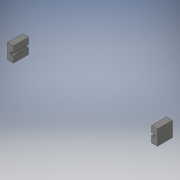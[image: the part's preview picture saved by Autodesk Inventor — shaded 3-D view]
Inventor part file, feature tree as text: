
AUTODESK INVENTOR PART (.ipt)
format: ipt  version: 2018 (Build 220112000, 112)  size: 122,368 bytes
history: native  units: in
note: dims shown in document units (in); Inventor stores cm internally (conversion verified against a paired STEP export)
features: extrude x1, sketch x1
ambient origin geometry x8: Origin, YZ Plane, XZ Plane, XY Plane, X Axis, Y Axis, Z Axis, Center Point
bodies: Solid1 (feature_tree)
feature tree (2):
  extrude  "Extrusion1"  Depth=0.0787in
  sketch  "Sketch1"  dims[d0=3.937in d1=0.0787in d2=3.7795in d3=0.1575in d4=0.0709in d5=0.3937in d6=0.0787in d7=3.622in d8=0.3937in d9=0.0in]
